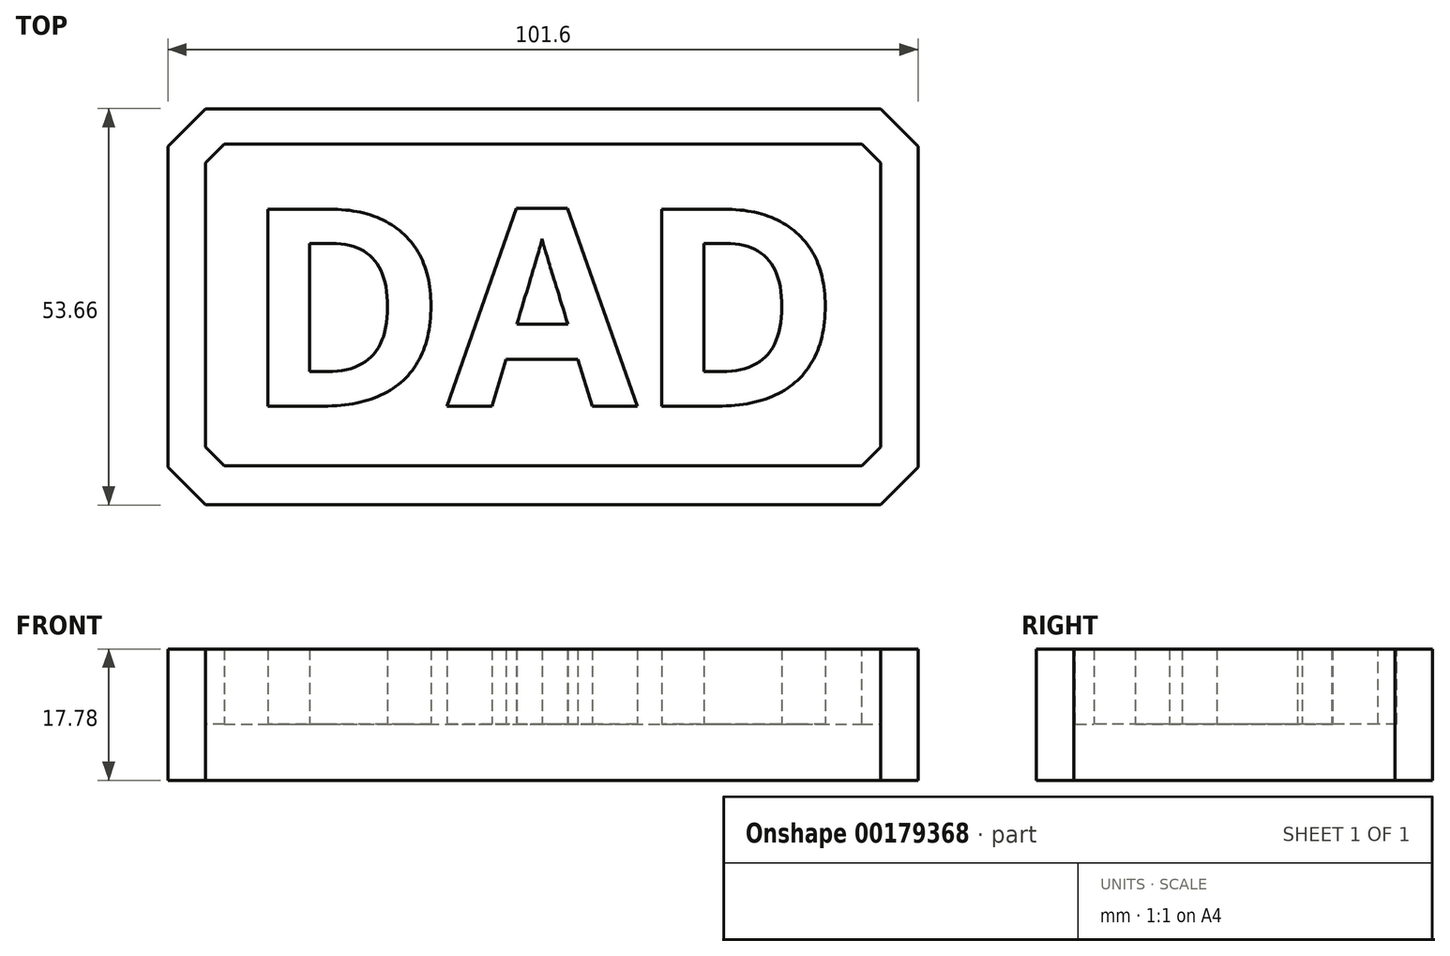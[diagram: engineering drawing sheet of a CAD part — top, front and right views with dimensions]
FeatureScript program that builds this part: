
annotation { "Feature Type Name" : "Feature", "Feature Type Description" : "" }
export const myFeature = defineFeature(function(context is Context, id is Id, definition is map)
    precondition{}
    {
        {
            var Q0;
            Q0=qCreatedBy(makeId("Top.planeOp"),FACE);
            var sketch = newSketch(context, id + "F0", { "sketchPlane" : qUnion([Q0])});
            skLineSegment(sketch, "E0.bottom", {"start": v(50.8, -26.83) * mm, "end": v(-50.8, -26.83) * mm});
            skLineSegment(sketch, "E0.top", {"start": v(50.8, 26.83) * mm, "end": v(-50.8, 26.83) * mm});
            skLineSegment(sketch, "E0.left", {"start": v(50.8, -26.83) * mm, "end": v(50.8, 26.83) * mm});
            skLineSegment(sketch, "E0.right", {"start": v(-50.8, -26.83) * mm, "end": v(-50.8, 26.83) * mm});
            skPoint(sketch, "E0.middle", {"position": v(0, 0) * mm});
            skSolve(sketch);
        }
        {
            var Q0;
            Q0=makeQuery(id+"F0.imprint","IMPRINT",FACE,{"disambiguationData":[TD([[makeQuery(id+"F0.imprint","IMPRINT",EDGE,{"derivedFrom":sQuery(id+"F0.wireOp",EDGE,"E0.bottom")}),-1.0]])]});
            extrude(context, id + "F1", {"entities" : qUnion([Q0]), "depth" : 7.62 * mm});
        }
        {
            var Q0;
            Q0=makeQuery(id+"F1.opExtrude","CAP_FACE",FACE,{"disambiguationData":[OSD([sQuery(id+"F0.wireOp",EDGE,"E0.bottom"),sQuery(id+"F0.wireOp",EDGE,"E0.top"),sQuery(id+"F0.wireOp",EDGE,"E0.left"),sQuery(id+"F0.wireOp",EDGE,"E0.right")])],"isStart":false});
            var sketch = newSketch(context, id + "F2", { "sketchPlane" : qUnion([Q0])});
            skText(sketch, "E1", { "text": "DAD", "fontName": "OpenSans-Bold.ttf"});
            skLineSegment(sketch, "E2.bottom", {"start": v(-45.72, 22.04) * mm, "end": v(45.72, 22.04) * mm});
            skLineSegment(sketch, "E2.top", {"start": v(-45.72, -21.54) * mm, "end": v(45.72, -21.54) * mm});
            skLineSegment(sketch, "E2.left", {"start": v(-45.72, 22.04) * mm, "end": v(-45.72, -21.54) * mm});
            skLineSegment(sketch, "E2.right", {"start": v(45.72, 22.04) * mm, "end": v(45.72, -21.54) * mm});
            const initialGuessF2  = {"E1": [-0.04064, -0.01344, 1, 0, 0.02688]};
            skSetInitialGuess(sketch, initialGuessF2);
            skSolve(sketch);
        }
        {
            var Q0;
            Q0=makeQuery(id+"F2.imprint","IMPRINT",FACE,{"disambiguationData":[TD([[makeQuery(id+"F2.imprint","IMPRINT",EDGE,{"derivedFrom":sQuery(id+"F2.wireOp",EDGE,"E2.bottom")}),1.0]])]});
            var Q1;
            Q1=makeQuery(id+"F2.imprint","IMPRINT",FACE,{"disambiguationData":[TD([[makeQuery(id+"F2.imprint","IMPRINT",EDGE,{"derivedFrom":sQuery(id+"F2.wireOp",EDGE,"E1.sketch_text.stroke-0")}),-1.0]])]});
            var Q2;
            Q2=makeQuery(id+"F2.imprint","IMPRINT",FACE,{"disambiguationData":[TD([[makeQuery(id+"F2.imprint","IMPRINT",EDGE,{"derivedFrom":sQuery(id+"F2.wireOp",EDGE,"E1.sketch_text.stroke-12")}),-1.0]])]});
            var Q3;
            Q3=makeQuery(id+"F2.imprint","IMPRINT",FACE,{"disambiguationData":[TD([[makeQuery(id+"F2.imprint","IMPRINT",EDGE,{"derivedFrom":sQuery(id+"F2.wireOp",EDGE,"E1.sketch_text.stroke-24")}),-1.0]])]});
            extrude(context, id + "F3", {"entities" : qUnion([Q0, Q1, Q2, Q3]), "operationType" : NewBodyOperationType.ADD, "depth" : 10.16 * mm});
        }
        {
            var Q0;
            {var subQ0=sQuery(id+"F0.wireOp",EDGE,"E0.right");var subQ1=sQuery(id+"F0.wireOp",EDGE,"E0.bottom");Q0=makeQuery(id+"F3.boolean.opBoolean","MERGE",EDGE,{"derivedFrom":[makeQuery(id+"F1.opExtrude","SWEPT_EDGE",EDGE,{"disambiguationData":[OSD([subQ1,subQ0])]}),makeQuery(id+"F3.opExtrude","SWEPT_EDGE",EDGE,{"disambiguationData":[OSD([subQ1,subQ0])]})]});}
            var Q1;
            {var subQ0=sQuery(id+"F0.wireOp",EDGE,"E0.right");var subQ1=sQuery(id+"F0.wireOp",EDGE,"E0.top");Q1=makeQuery(id+"F3.boolean.opBoolean","MERGE",EDGE,{"derivedFrom":[makeQuery(id+"F1.opExtrude","SWEPT_EDGE",EDGE,{"disambiguationData":[OSD([subQ1,subQ0])]}),makeQuery(id+"F3.opExtrude","SWEPT_EDGE",EDGE,{"disambiguationData":[OSD([subQ1,subQ0])]})]});}
            var Q2;
            {var subQ0=sQuery(id+"F0.wireOp",EDGE,"E0.left");var subQ1=sQuery(id+"F0.wireOp",EDGE,"E0.bottom");Q2=makeQuery(id+"F3.boolean.opBoolean","MERGE",EDGE,{"derivedFrom":[makeQuery(id+"F1.opExtrude","SWEPT_EDGE",EDGE,{"disambiguationData":[OSD([subQ1,subQ0])]}),makeQuery(id+"F3.opExtrude","SWEPT_EDGE",EDGE,{"disambiguationData":[OSD([subQ1,subQ0])]})]});}
            var Q3;
            {var subQ0=sQuery(id+"F0.wireOp",EDGE,"E0.left");var subQ1=sQuery(id+"F0.wireOp",EDGE,"E0.top");Q3=makeQuery(id+"F3.boolean.opBoolean","MERGE",EDGE,{"derivedFrom":[makeQuery(id+"F1.opExtrude","SWEPT_EDGE",EDGE,{"disambiguationData":[OSD([subQ1,subQ0])]}),makeQuery(id+"F3.opExtrude","SWEPT_EDGE",EDGE,{"disambiguationData":[OSD([subQ1,subQ0])]})]});}
            chamfer(context, id + "F4", {"entities" : qUnion([Q0, Q1, Q2, Q3]), "width" : 5.08 * mm, "tangentPropagation" : true});
        }
        {
            var Q0;
            Q0=makeQuery(id+"F3.opExtrude","SWEPT_EDGE",EDGE,{"disambiguationData":[OSD([sQuery(id+"F2.wireOp",EDGE,"E2.bottom"),sQuery(id+"F2.wireOp",EDGE,"E2.right")])]});
            var Q1;
            Q1=makeQuery(id+"F3.opExtrude","SWEPT_EDGE",EDGE,{"disambiguationData":[OSD([sQuery(id+"F2.wireOp",EDGE,"E2.top"),sQuery(id+"F2.wireOp",EDGE,"E2.right")])]});
            var Q2;
            Q2=makeQuery(id+"F3.opExtrude","SWEPT_EDGE",EDGE,{"disambiguationData":[OSD([sQuery(id+"F2.wireOp",EDGE,"E2.bottom"),sQuery(id+"F2.wireOp",EDGE,"E2.left")])]});
            var Q3;
            Q3=makeQuery(id+"F3.opExtrude","SWEPT_EDGE",EDGE,{"disambiguationData":[OSD([sQuery(id+"F2.wireOp",EDGE,"E2.top"),sQuery(id+"F2.wireOp",EDGE,"E2.left")])]});
            chamfer(context, id + "F5", {"entities" : qUnion([Q0, Q1, Q2, Q3]), "width" : 2.54 * mm, "tangentPropagation" : true});
        }
    });
